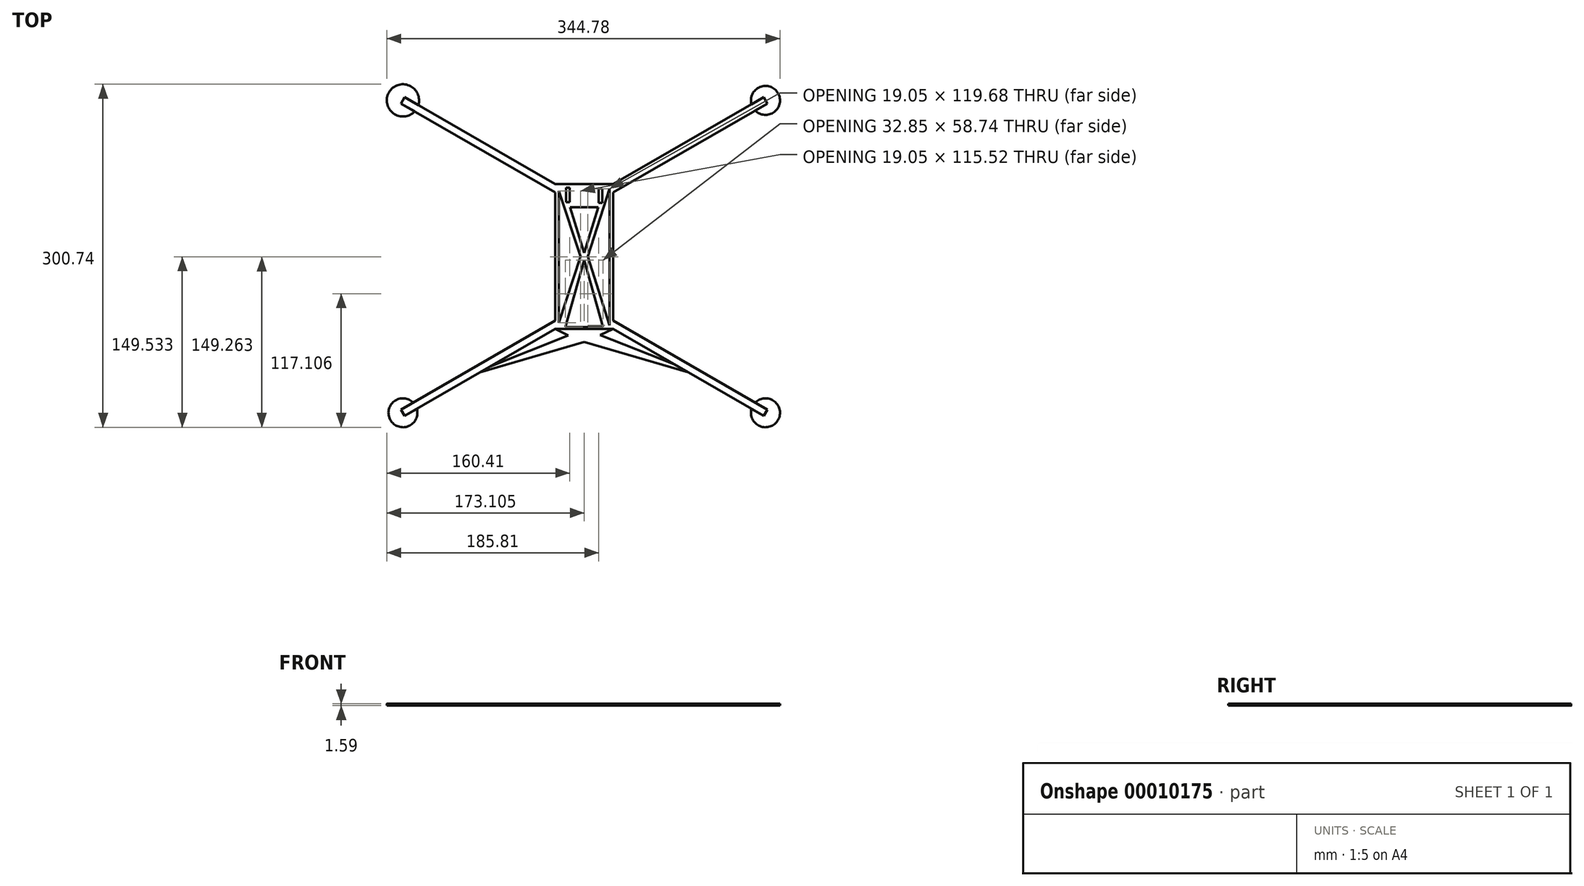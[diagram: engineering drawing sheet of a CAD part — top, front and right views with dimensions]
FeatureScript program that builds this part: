
annotation { "Feature Type Name" : "Feature", "Feature Type Description" : "" }
export const myFeature = defineFeature(function(context is Context, id is Id, definition is map)
    precondition{}
    {
        {
            var Q0;
            Q0=qCreatedBy(makeId("Top.planeOp"),FACE);
            var sketch = newSketch(context, id + "F0", { "sketchPlane" : qUnion([Q0])});
            skLineSegment(sketch, "E0.rect.bottom", {"start": v(25.4, 63.5) * mm, "end": v(-25.4, 63.5) * mm});
            skLineSegment(sketch, "E0.rect.top", {"start": v(25.4, -63.5) * mm, "end": v(-25.4, -63.5) * mm});
            skLineSegment(sketch, "E0.rect.left", {"start": v(25.4, 63.5) * mm, "end": v(25.4, -63.5) * mm});
            skLineSegment(sketch, "E0.rect.right", {"start": v(-25.4, 63.5) * mm, "end": v(-25.4, -63.5) * mm});
            skPoint(sketch, "E0.rect.middle", {"position": v(0, 0) * mm});
            skLineSegment(sketch, "E1", {"start": v(0, 0) * mm, "end": v(25.4, 63.5) * mm});
            skLineSegment(sketch, "E2", {"start": v(25.4, 63.5) * mm, "end": v(157.38, 139.7) * mm});
            skLineSegment(sketch, "E3", {"start": v(-25.4, 63.5) * mm, "end": v(-157.38, 139.7) * mm});
            skLineSegment(sketch, "E4", {"start": v(-25.4, -63.5) * mm, "end": v(-157.38, -139.7) * mm});
            skLineSegment(sketch, "E5", {"start": v(25.4, -63.5) * mm, "end": v(157.38, -139.7) * mm});
            skLineSegment(sketch, "E6", {"start": v(-157.38, 139.7) * mm, "end": v(-160.56, 134.2) * mm});
            skLineSegment(sketch, "E7", {"start": v(-160.56, 134.2) * mm, "end": v(-25.4, 56.17) * mm});
            skLineSegment(sketch, "E8", {"start": v(-157.38, -139.7) * mm, "end": v(-160.56, -134.2) * mm});
            skLineSegment(sketch, "E9", {"start": v(-160.56, -134.2) * mm, "end": v(-25.4, -56.17) * mm});
            skLineSegment(sketch, "E10", {"start": v(157.38, -139.7) * mm, "end": v(160.56, -134.2) * mm});
            skLineSegment(sketch, "E11", {"start": v(160.56, -134.2) * mm, "end": v(25.4, -56.17) * mm});
            skLineSegment(sketch, "E12", {"start": v(157.38, 139.7) * mm, "end": v(160.56, 134.2) * mm});
            skLineSegment(sketch, "E13", {"start": v(160.56, 134.2) * mm, "end": v(25.4, 56.17) * mm});
            skSolve(sketch);
        }
        {
            var Q0;
            {var subQ1=sQuery(id+"F0.wireOp",EDGE,"E2");Q0=makeQuery(id+"F0.imprint","IMPRINT",FACE,{"disambiguationData":[TD([[makeQuery(id+"F0.imprint","IMPRINT",EDGE,{"derivedFrom":subQ1}),-1.0]])]});}
            var Q1;
            {var subQ1=sQuery(id+"F0.wireOp",EDGE,"E5");Q1=makeQuery(id+"F0.imprint","IMPRINT",FACE,{"disambiguationData":[TD([[makeQuery(id+"F0.imprint","IMPRINT",EDGE,{"derivedFrom":subQ1}),1.0]])]});}
            var Q2;
            {var subQ1=sQuery(id+"F0.wireOp",EDGE,"E3");Q2=makeQuery(id+"F0.imprint","IMPRINT",FACE,{"disambiguationData":[TD([[makeQuery(id+"F0.imprint","IMPRINT",EDGE,{"derivedFrom":subQ1}),1.0]])]});}
            var Q3;
            {var subQ1=sQuery(id+"F0.wireOp",EDGE,"E4");Q3=makeQuery(id+"F0.imprint","IMPRINT",FACE,{"disambiguationData":[TD([[makeQuery(id+"F0.imprint","IMPRINT",EDGE,{"derivedFrom":subQ1}),-1.0]])]});}
            var Q4;
            {var subQ3=sQuery(id+"F0.wireOp",EDGE,"E0.rect.bottom");Q4=makeQuery(id+"F0.imprint","IMPRINT",FACE,{"disambiguationData":[TD([[makeQuery(id+"F0.imprint","IMPRINT",EDGE,{"derivedFrom":subQ3}),1.0]])]});}
            extrude(context, id + "F1", {"entities" : qUnion([Q0, Q1, Q2, Q3, Q4]), "depth" : 1.59 * mm});
        }
        {
            var Q0;
            Q0=makeQuery(id+"F1.opExtrude","CAP_FACE",FACE,{"disambiguationData":[OSD([sQuery(id+"F0.wireOp",EDGE,"E0.rect.bottom"),sQuery(id+"F0.wireOp",EDGE,"E0.rect.top"),sQuery(id+"F0.wireOp",EDGE,"E0.rect.left"),sQuery(id+"F0.wireOp",EDGE,"E0.rect.right"),sQuery(id+"F0.wireOp",EDGE,"E2"),sQuery(id+"F0.wireOp",EDGE,"E3"),sQuery(id+"F0.wireOp",EDGE,"E4"),sQuery(id+"F0.wireOp",EDGE,"E5"),sQuery(id+"F0.wireOp",EDGE,"E6"),sQuery(id+"F0.wireOp",EDGE,"E7"),sQuery(id+"F0.wireOp",EDGE,"E8"),sQuery(id+"F0.wireOp",EDGE,"E9"),sQuery(id+"F0.wireOp",EDGE,"E10"),sQuery(id+"F0.wireOp",EDGE,"E11"),sQuery(id+"F0.wireOp",EDGE,"E12"),sQuery(id+"F0.wireOp",EDGE,"E13")])],"isStart":false});
            var sketch = newSketch(context, id + "F2", { "sketchPlane" : qUnion([Q0])});
            skLineSegment(sketch, "E14", {"start": v(-22.23, 57.65) * mm, "end": v(-22.22, -57.88) * mm});
            skLineSegment(sketch, "E15", {"start": v(-22.23, -57.88) * mm, "end": v(-3.17, 0) * mm});
            skLineSegment(sketch, "E16", {"start": v(-3.17, 0) * mm, "end": v(-22.23, 57.65) * mm});
            skLineSegment(sketch, "E17", {"start": v(22.23, -60.23) * mm, "end": v(22.23, 59.45) * mm});
            skLineSegment(sketch, "E18", {"start": v(22.22, 59.45) * mm, "end": v(3.17, 0) * mm});
            skLineSegment(sketch, "E19", {"start": v(3.17, 0) * mm, "end": v(22.23, -60.23) * mm});
            skLineSegment(sketch, "E20", {"start": v(-16.43, -61.91) * mm, "end": v(16.42, -61.91) * mm});
            skLineSegment(sketch, "E21", {"start": v(16.42, -61.91) * mm, "end": v(0, -3.17) * mm});
            skLineSegment(sketch, "E22", {"start": v(0, -3.18) * mm, "end": v(-16.43, -61.91) * mm});
            skLineSegment(sketch, "E23", {"start": v(0, 3.18) * mm, "end": v(12.45, 43.25) * mm});
            skLineSegment(sketch, "E24", {"start": v(12.45, 43.25) * mm, "end": v(-12.28, 43.25) * mm});
            skLineSegment(sketch, "E25", {"start": v(-12.28, 43.25) * mm, "end": v(0, 3.18) * mm});
            skLineSegment(sketch, "E26.bottom", {"start": v(-15.88, 60.4) * mm, "end": v(-12.7, 60.4) * mm});
            skLineSegment(sketch, "E26.top", {"start": v(-15.88, 47.7) * mm, "end": v(-12.7, 47.7) * mm});
            skLineSegment(sketch, "E26.left", {"start": v(-15.88, 60.4) * mm, "end": v(-15.88, 47.7) * mm});
            skLineSegment(sketch, "E26.right", {"start": v(-12.7, 60.4) * mm, "end": v(-12.7, 47.7) * mm});
            skLineSegment(sketch, "E27.bottom", {"start": v(12.7, 59.62) * mm, "end": v(15.88, 59.62) * mm});
            skLineSegment(sketch, "E27.top", {"start": v(12.7, 46.92) * mm, "end": v(15.88, 46.92) * mm});
            skLineSegment(sketch, "E27.left", {"start": v(12.7, 59.62) * mm, "end": v(12.7, 46.92) * mm});
            skLineSegment(sketch, "E27.right", {"start": v(15.88, 59.62) * mm, "end": v(15.88, 46.92) * mm});
            skSolve(sketch);
        }
        {
            var Q0;
            Q0=makeQuery(id+"F2.imprint","IMPRINT",FACE,{"disambiguationData":[TD([[makeQuery(id+"F2.imprint","IMPRINT",EDGE,{"derivedFrom":sQuery(id+"F2.wireOp",EDGE,"E14")}),1.0]])]});
            var Q1;
            Q1=makeQuery(id+"F2.imprint","IMPRINT",FACE,{"disambiguationData":[TD([[makeQuery(id+"F2.imprint","IMPRINT",EDGE,{"derivedFrom":sQuery(id+"F2.wireOp",EDGE,"E23")}),1.0]])]});
            var Q2;
            Q2=makeQuery(id+"F2.imprint","IMPRINT",FACE,{"disambiguationData":[TD([[makeQuery(id+"F2.imprint","IMPRINT",EDGE,{"derivedFrom":sQuery(id+"F2.wireOp",EDGE,"E26.bottom")}),-1.0]])]});
            var Q3;
            Q3=makeQuery(id+"F2.imprint","IMPRINT",FACE,{"disambiguationData":[TD([[makeQuery(id+"F2.imprint","IMPRINT",EDGE,{"derivedFrom":sQuery(id+"F2.wireOp",EDGE,"E27.bottom")}),-1.0]])]});
            var Q4;
            Q4=makeQuery(id+"F2.imprint","IMPRINT",FACE,{"disambiguationData":[TD([[makeQuery(id+"F2.imprint","IMPRINT",EDGE,{"derivedFrom":sQuery(id+"F2.wireOp",EDGE,"E17")}),1.0]])]});
            var Q5;
            Q5=makeQuery(id+"F2.imprint","IMPRINT",FACE,{"disambiguationData":[TD([[makeQuery(id+"F2.imprint","IMPRINT",EDGE,{"derivedFrom":sQuery(id+"F2.wireOp",EDGE,"E20")}),1.0]])]});
            extrude(context, id + "F3", {"entities" : qUnion([Q0, Q1, Q2, Q3, Q4, Q5]), "operationType" : NewBodyOperationType.REMOVE, "oppositeDirection" : true, "depth" : 1.59 * mm});
        }
        {
            var Q0;
            Q0=makeQuery(id+"F1.opExtrude","CAP_FACE",FACE,{"disambiguationData":[OSD([sQuery(id+"F0.wireOp",EDGE,"E0.rect.bottom"),sQuery(id+"F0.wireOp",EDGE,"E0.rect.top"),sQuery(id+"F0.wireOp",EDGE,"E0.rect.left"),sQuery(id+"F0.wireOp",EDGE,"E0.rect.right"),sQuery(id+"F0.wireOp",EDGE,"E2"),sQuery(id+"F0.wireOp",EDGE,"E3"),sQuery(id+"F0.wireOp",EDGE,"E4"),sQuery(id+"F0.wireOp",EDGE,"E5"),sQuery(id+"F0.wireOp",EDGE,"E6"),sQuery(id+"F0.wireOp",EDGE,"E7"),sQuery(id+"F0.wireOp",EDGE,"E8"),sQuery(id+"F0.wireOp",EDGE,"E9"),sQuery(id+"F0.wireOp",EDGE,"E10"),sQuery(id+"F0.wireOp",EDGE,"E11"),sQuery(id+"F0.wireOp",EDGE,"E12"),sQuery(id+"F0.wireOp",EDGE,"E13")])],"isStart":false});
            var sketch = newSketch(context, id + "F4", { "sketchPlane" : qUnion([Q0])});
            skLineSegment(sketch, "E28", {"start": v(-82.55, -96.5) * mm, "end": v(0, -63.5) * mm});
            skLineSegment(sketch, "E29", {"start": v(0, -63.5) * mm, "end": v(78.48, -94.14) * mm});
            skLineSegment(sketch, "E30", {"start": v(91.4, -101.6) * mm, "end": v(0, -74.76) * mm});
            skLineSegment(sketch, "E31", {"start": v(0, -74.76) * mm, "end": v(-91.4, -101.6) * mm});
            skLineSegment(sketch, "E32", {"start": v(-14, -69.1) * mm, "end": v(-25.4, -63.5) * mm});
            skLineSegment(sketch, "E33", {"start": v(13.92, -68.94) * mm, "end": v(25.4, -63.5) * mm});
            skSolve(sketch);
        }
        {
            var Q0;
            Q0 = qSketchRegion(id + "F4", true);
            var Q1;
            {var subQ1=sQuery(id+"F4.wireOp",EDGE,"E30");Q1=makeQuery(id+"F4.imprint","IMPRINT",FACE,{"disambiguationData":[TD([[makeQuery(id+"F4.imprint","IMPRINT",EDGE,{"derivedFrom":subQ1}),-1.0]])]});}
            var Q2;
            {var subQ3=sQuery(id+"F4.wireOp",EDGE,"E32");Q2=makeQuery(id+"F4.imprint","IMPRINT",FACE,{"disambiguationData":[TD([[makeQuery(id+"F4.imprint","IMPRINT",EDGE,{"derivedFrom":subQ3}),-1.0]])]});}
            var Q3;
            {var subQ3=sQuery(id+"F4.wireOp",EDGE,"E33");Q3=makeQuery(id+"F4.imprint","IMPRINT",FACE,{"disambiguationData":[TD([[makeQuery(id+"F4.imprint","IMPRINT",EDGE,{"derivedFrom":subQ3}),1.0]])]});}
            extrude(context, id + "F5", {"entities" : qUnion([Q0, Q1, Q2, Q3]), "oppositeDirection" : true, "depth" : 1.59 * mm});
        }
        {
            var Q0;
            Q0=makeQuery(id+"F1.opExtrude","CAP_FACE",FACE,{"disambiguationData":[OSD([sQuery(id+"F0.wireOp",EDGE,"E0.rect.bottom"),sQuery(id+"F0.wireOp",EDGE,"E0.rect.top"),sQuery(id+"F0.wireOp",EDGE,"E0.rect.left"),sQuery(id+"F0.wireOp",EDGE,"E0.rect.right"),sQuery(id+"F0.wireOp",EDGE,"E2"),sQuery(id+"F0.wireOp",EDGE,"E3"),sQuery(id+"F0.wireOp",EDGE,"E4"),sQuery(id+"F0.wireOp",EDGE,"E5"),sQuery(id+"F0.wireOp",EDGE,"E6"),sQuery(id+"F0.wireOp",EDGE,"E7"),sQuery(id+"F0.wireOp",EDGE,"E8"),sQuery(id+"F0.wireOp",EDGE,"E9"),sQuery(id+"F0.wireOp",EDGE,"E10"),sQuery(id+"F0.wireOp",EDGE,"E11"),sQuery(id+"F0.wireOp",EDGE,"E12"),sQuery(id+"F0.wireOp",EDGE,"E13")])],"isStart":false});
            var sketch = newSketch(context, id + "F6", { "sketchPlane" : qUnion([Q0])});
            skCircle(sketch, "E34", {"center": v(-158.97, 136.95) * mm, "radius": 14.14 * mm});
            skCircle(sketch, "E35", {"center": v(158.97, 136.95) * mm, "radius": 12.7 * mm});
            skCircle(sketch, "E36", {"center": v(158.97, -136.95) * mm, "radius": 12.7 * mm});
            skCircle(sketch, "E37", {"center": v(-158.97, -136.95) * mm, "radius": 12.7 * mm});
            skSolve(sketch);
        }
        {
            var Q0;
            {var subQ3=makeQuery(id+"F1.opExtrude","CAP_EDGE",EDGE,{"disambiguationData":[OSD([sQuery(id+"F0.wireOp",EDGE,"E6")])],"isStart":false});Q0=makeQuery(id+"F6.imprint","IMPRINT",FACE,{"disambiguationData":[TD([[makeQuery(id+"F6.imprint","IMPRINT",EDGE,{"derivedFrom":subQ3}),-1.0]])]});}
            var Q1;
            {var subQ3=makeQuery(id+"F1.opExtrude","CAP_EDGE",EDGE,{"disambiguationData":[OSD([sQuery(id+"F0.wireOp",EDGE,"E8")])],"isStart":false});Q1=makeQuery(id+"F6.imprint","IMPRINT",FACE,{"disambiguationData":[TD([[makeQuery(id+"F6.imprint","IMPRINT",EDGE,{"derivedFrom":subQ3}),1.0]])]});}
            var Q2;
            {var subQ3=makeQuery(id+"F1.opExtrude","CAP_EDGE",EDGE,{"disambiguationData":[OSD([sQuery(id+"F0.wireOp",EDGE,"E10")])],"isStart":false});Q2=makeQuery(id+"F6.imprint","IMPRINT",FACE,{"disambiguationData":[TD([[makeQuery(id+"F6.imprint","IMPRINT",EDGE,{"derivedFrom":subQ3}),-1.0]])]});}
            var Q3;
            {var subQ3=makeQuery(id+"F1.opExtrude","CAP_EDGE",EDGE,{"disambiguationData":[OSD([sQuery(id+"F0.wireOp",EDGE,"E12")])],"isStart":false});Q3=makeQuery(id+"F6.imprint","IMPRINT",FACE,{"disambiguationData":[TD([[makeQuery(id+"F6.imprint","IMPRINT",EDGE,{"derivedFrom":subQ3}),1.0]])]});}
            extrude(context, id + "F7", {"entities" : qUnion([Q0, Q1, Q2, Q3]), "oppositeDirection" : true, "depth" : 1.59 * mm});
        }
    });
